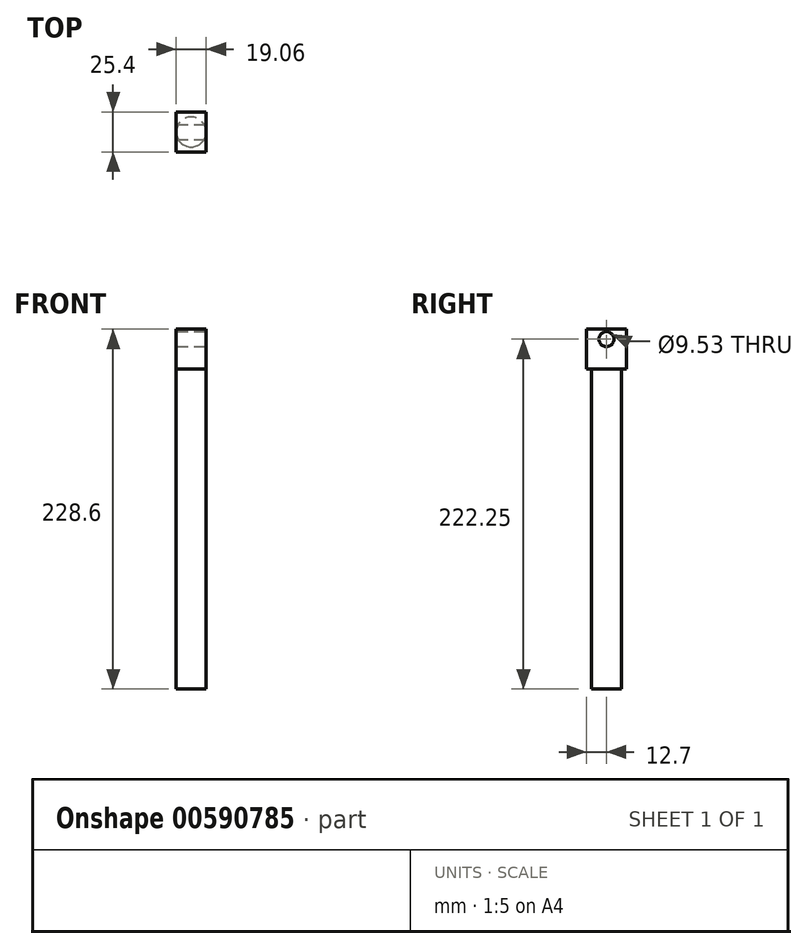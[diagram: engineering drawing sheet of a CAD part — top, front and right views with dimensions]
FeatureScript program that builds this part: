
annotation { "Feature Type Name" : "Feature", "Feature Type Description" : "" }
export const myFeature = defineFeature(function(context is Context, id is Id, definition is map)
    precondition{}
    {
        {
            var Q0;
            Q0=qCreatedBy(makeId("Top.planeOp"),FACE);
            var sketch = newSketch(context, id + "F0", { "sketchPlane" : qUnion([Q0])});
            skCircle(sketch, "E0", {"center": v(0, 0) * mm, "radius": 9.53 * mm});
            skSolve(sketch);
        }
        {
            var Q0;
            Q0 = qSketchRegion(id + "F0", true);
            extrude(context, id + "F1", {"entities" : qUnion([Q0]), "depth" : 203.2 * mm, "offsetDistance" : 25.4 * mm});
        }
        {
            var Q0;
            Q0=makeQuery(id+"F1.opExtrude","CAP_FACE",FACE,{"disambiguationData":[OSD([sQuery(id+"F0.wireOp",EDGE,"E0")])],"isStart":false});
            var sketch = newSketch(context, id + "F2", { "sketchPlane" : qUnion([Q0])});
            skLineSegment(sketch, "E1.bottom", {"start": v(9.52, 12.7) * mm, "end": v(-9.53, 12.7) * mm});
            skLineSegment(sketch, "E1.top", {"start": v(9.53, -12.7) * mm, "end": v(-9.52, -12.7) * mm});
            skLineSegment(sketch, "E1.left", {"start": v(9.52, 12.7) * mm, "end": v(9.53, -12.7) * mm});
            skLineSegment(sketch, "E1.right", {"start": v(-9.53, 12.7) * mm, "end": v(-9.52, -12.7) * mm});
            skPoint(sketch, "E1.middle", {"position": v(0, 0) * mm});
            skSolve(sketch);
        }
        {
            var Q0;
            Q0 = qSketchRegion(id + "F2", true);
            extrude(context, id + "F3", {"entities" : qUnion([Q0]), "operationType" : NewBodyOperationType.ADD, "depth" : 25.4 * mm, "offsetDistance" : 25.4 * mm});
        }
        {
            var Q0;
            Q0=makeQuery(id+"F3.opExtrude","SWEPT_FACE",FACE,{"disambiguationData":[OSD([sQuery(id+"F2.wireOp",EDGE,"E1.left")])]});
            var sketch = newSketch(context, id + "F4", { "sketchPlane" : qUnion([Q0])});
            skCircle(sketch, "E2", {"center": v(0, 222.25) * mm, "radius": 4.76 * mm});
            skPoint(sketch, "E2.centerSnap0", {"position": v(0, 228.6) * mm});
            skSolve(sketch);
        }
        {
            var Q0;
            Q0 = qSketchRegion(id + "F4", true);
            extrude(context, id + "F5", {"entities" : qUnion([Q0]), "operationType" : NewBodyOperationType.REMOVE, "endBound" : BoundingType.THROUGH_ALL, "oppositeDirection" : true, "depth" : 25.4 * mm, "offsetDistance" : 25.4 * mm});
        }
    });
